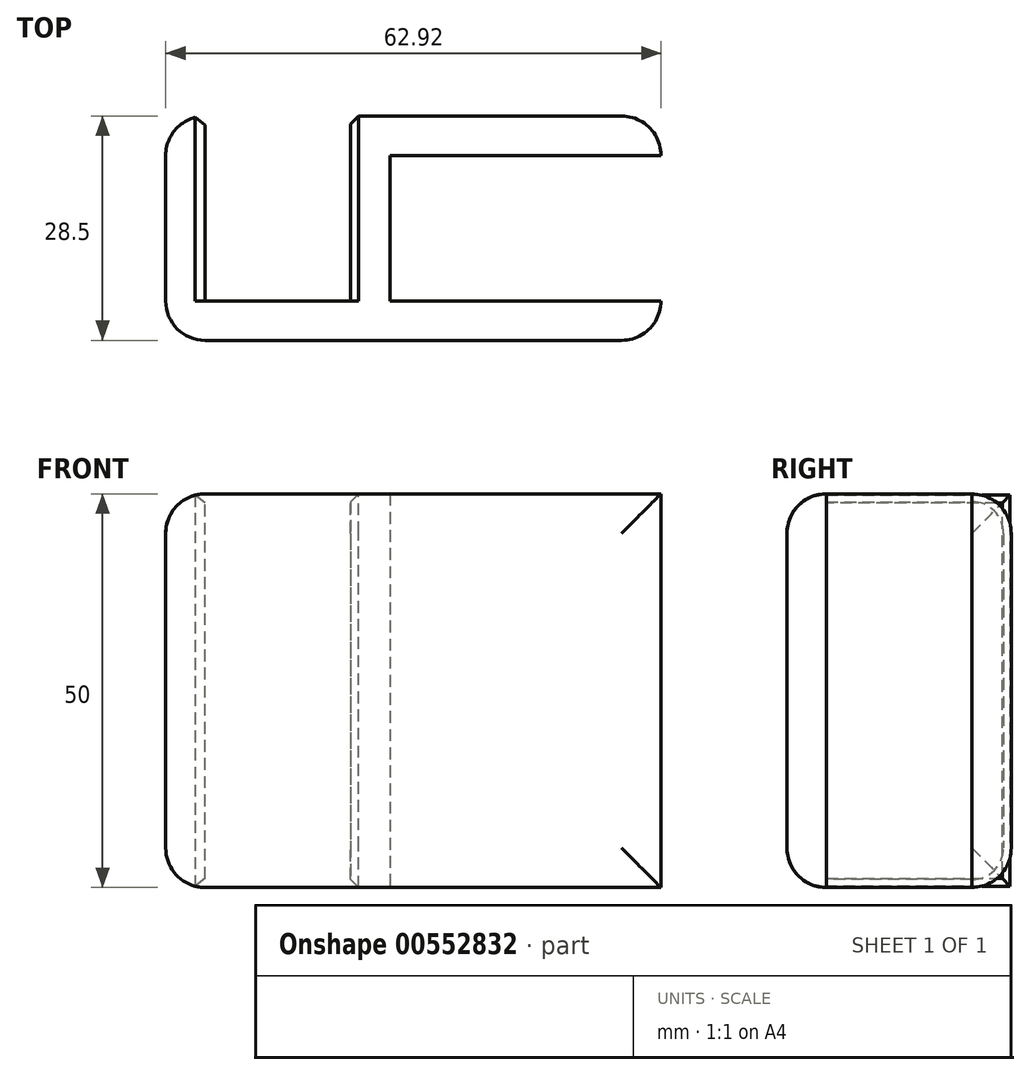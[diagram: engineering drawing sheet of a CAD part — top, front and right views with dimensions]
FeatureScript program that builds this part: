
annotation { "Feature Type Name" : "Feature", "Feature Type Description" : "" }
export const myFeature = defineFeature(function(context is Context, id is Id, definition is map)
    precondition{}
    {
        {
            var Q0;
            Q0=qCreatedBy(makeId("Top.planeOp"),FACE);
            var sketch = newSketch(context, id + "F0", { "sketchPlane" : qUnion([Q0])});
            skLineSegment(sketch, "E0", {"start": v(29.43, 14.2) * mm, "end": v(-9.99, 14.2) * mm});
            skLineSegment(sketch, "E1", {"start": v(-9.99, 14.2) * mm, "end": v(-9.99, -9.3) * mm});
            skLineSegment(sketch, "E2", {"start": v(-9.99, -9.3) * mm, "end": v(-28.49, -9.3) * mm});
            skLineSegment(sketch, "E3", {"start": v(-28.49, -9.3) * mm, "end": v(-28.49, 14.2) * mm});
            skLineSegment(sketch, "E4", {"start": v(-28.49, 14.2) * mm, "end": v(-33.49, 14.2) * mm});
            skLineSegment(sketch, "E5", {"start": v(-33.49, 14.2) * mm, "end": v(-33.49, -14.3) * mm});
            skLineSegment(sketch, "E6", {"start": v(-33.49, -14.3) * mm, "end": v(29.43, -14.3) * mm});
            skLineSegment(sketch, "E7", {"start": v(29.43, -14.3) * mm, "end": v(29.43, -9.3) * mm});
            skLineSegment(sketch, "E8", {"start": v(29.43, -9.3) * mm, "end": v(-4.99, -9.3) * mm});
            skLineSegment(sketch, "E9", {"start": v(-4.99, -9.3) * mm, "end": v(-4.99, 9.2) * mm});
            skLineSegment(sketch, "E10", {"start": v(-4.99, 9.2) * mm, "end": v(29.43, 9.2) * mm});
            skLineSegment(sketch, "E11", {"start": v(29.43, 9.2) * mm, "end": v(29.43, 14.2) * mm});
            skSolve(sketch);
        }
        {
            var Q0;
            Q0=makeQuery(id+"F0.imprint","IMPRINT",FACE,{"disambiguationData":[TD([[makeQuery(id+"F0.imprint","IMPRINT",EDGE,{"derivedFrom":sQuery(id+"F0.wireOp",EDGE,"E0")}),1.0]])]});
            extrude(context, id + "F1", {"entities" : qUnion([Q0]), "depth" : 50 * mm, "offsetDistance" : 25 * mm});
        }
        {
            var Q0;
            Q0=makeQuery(id+"F1.opExtrude","SWEPT_EDGE",EDGE,{"disambiguationData":[OSD([sQuery(id+"F0.wireOp",EDGE,"E4"),sQuery(id+"F0.wireOp",EDGE,"E5")])]});
            var Q1;
            Q1=makeQuery(id+"F1.opExtrude","CAP_EDGE",EDGE,{"disambiguationData":[OSD([sQuery(id+"F0.wireOp",EDGE,"E5")])],"isStart":true});
            var Q2;
            Q2=makeQuery(id+"F1.opExtrude","SWEPT_EDGE",EDGE,{"disambiguationData":[OSD([sQuery(id+"F0.wireOp",EDGE,"E5"),sQuery(id+"F0.wireOp",EDGE,"E6")])]});
            var Q3;
            Q3=makeQuery(id+"F1.opExtrude","CAP_EDGE",EDGE,{"disambiguationData":[OSD([sQuery(id+"F0.wireOp",EDGE,"E5")])],"isStart":false});
            var Q4;
            Q4=makeQuery(id+"F1.opExtrude","CAP_EDGE",EDGE,{"disambiguationData":[OSD([sQuery(id+"F0.wireOp",EDGE,"E6")])],"isStart":false});
            var Q5;
            Q5=makeQuery(id+"F1.opExtrude","CAP_EDGE",EDGE,{"disambiguationData":[OSD([sQuery(id+"F0.wireOp",EDGE,"E6")])],"isStart":true});
            var Q6;
            Q6=makeQuery(id+"F1.opExtrude","SWEPT_EDGE",EDGE,{"disambiguationData":[OSD([sQuery(id+"F0.wireOp",EDGE,"E6"),sQuery(id+"F0.wireOp",EDGE,"E7")])]});
            var Q7;
            Q7=makeQuery(id+"F1.opExtrude","CAP_EDGE",EDGE,{"disambiguationData":[OSD([sQuery(id+"F0.wireOp",EDGE,"E0")])],"isStart":true});
            var Q8;
            Q8=makeQuery(id+"F1.opExtrude","SWEPT_EDGE",EDGE,{"disambiguationData":[OSD([sQuery(id+"F0.wireOp",EDGE,"E0"),sQuery(id+"F0.wireOp",EDGE,"E11")])]});
            var Q9;
            Q9=makeQuery(id+"F1.opExtrude","CAP_EDGE",EDGE,{"disambiguationData":[OSD([sQuery(id+"F0.wireOp",EDGE,"E0")])],"isStart":false});
            fillet(context, id + "F2", {"entities" : qUnion([Q0, Q1, Q2, Q3, Q4, Q5, Q6, Q7, Q8, Q9]), "radius" : 5 * mm, "tangentPropagation" : true, "allowEdgeOverflow" : false});
        }
        {
            var Q0;
            Q0=makeQuery(id+"F1.opExtrude","SWEPT_EDGE",EDGE,{"disambiguationData":[OSD([sQuery(id+"F0.wireOp",EDGE,"E0"),sQuery(id+"F0.wireOp",EDGE,"E1")])]});
            var Q1;
            Q1=makeQuery(id+"F2.opFillet","BLEND_EDGE",EDGE,{"blendedFrom":[makeQuery(id+"F1.opExtrude","SWEPT_EDGE",EDGE,{"disambiguationData":[OSD([sQuery(id+"F0.wireOp",EDGE,"E4"),sQuery(id+"F0.wireOp",EDGE,"E5")])]}),makeQuery(id+"F1.opExtrude","SWEPT_FACE",FACE,{"disambiguationData":[OSD([sQuery(id+"F0.wireOp",EDGE,"E3")])]})],"blendedInto":[makeQuery(id+"F1.opExtrude","SWEPT_FACE",FACE,{"disambiguationData":[OSD([sQuery(id+"F0.wireOp",EDGE,"E3")])]})]});
            var Q2;
            Q2=makeQuery(id+"F2.opFillet","BLEND_EDGE",EDGE,{"blendedFrom":[makeQuery(id+"F1.opExtrude","CAP_EDGE",EDGE,{"disambiguationData":[OSD([sQuery(id+"F0.wireOp",EDGE,"E5")])],"isStart":false}),makeQuery(id+"F1.opExtrude","SWEPT_FACE",FACE,{"disambiguationData":[OSD([sQuery(id+"F0.wireOp",EDGE,"E3")])]})],"blendedInto":[makeQuery(id+"F1.opExtrude","SWEPT_FACE",FACE,{"disambiguationData":[OSD([sQuery(id+"F0.wireOp",EDGE,"E3")])]})]});
            var Q3;
            Q3=makeQuery(id+"F2.opFillet","BLEND_EDGE",EDGE,{"blendedFrom":[makeQuery(id+"F1.opExtrude","CAP_EDGE",EDGE,{"disambiguationData":[OSD([sQuery(id+"F0.wireOp",EDGE,"E5")])],"isStart":true}),makeQuery(id+"F1.opExtrude","SWEPT_FACE",FACE,{"disambiguationData":[OSD([sQuery(id+"F0.wireOp",EDGE,"E3")])]})],"blendedInto":[makeQuery(id+"F1.opExtrude","SWEPT_FACE",FACE,{"disambiguationData":[OSD([sQuery(id+"F0.wireOp",EDGE,"E3")])]})]});
            chamfer(context, id + "F3", {"entities" : qUnion([Q0, Q1, Q2, Q3]), "width" : 1 * mm, "tangentPropagation" : true});
        }
    });
